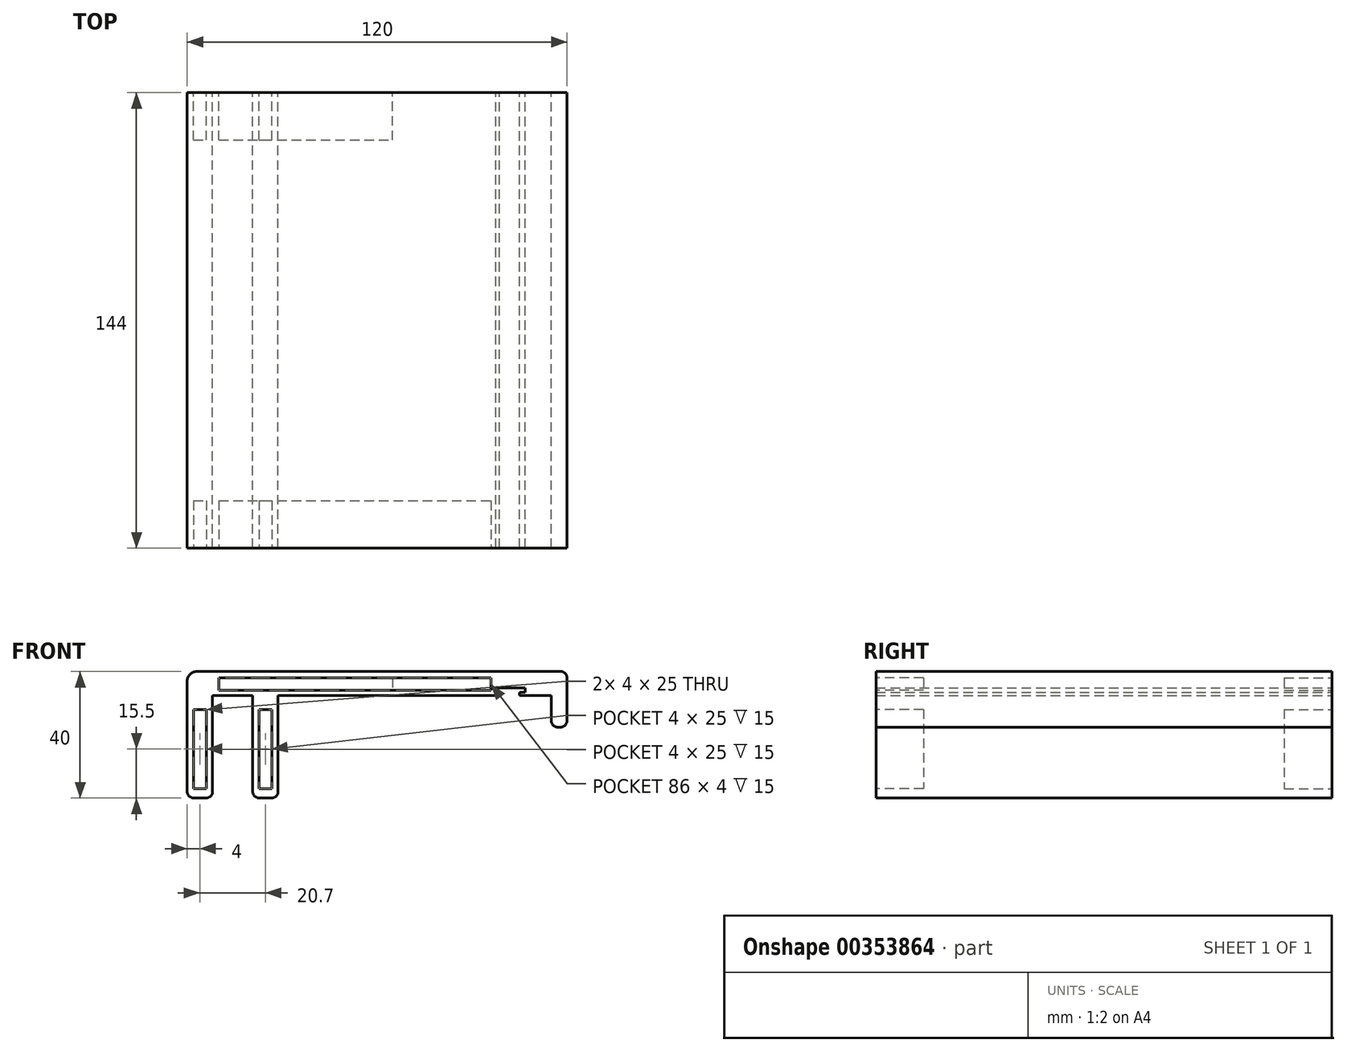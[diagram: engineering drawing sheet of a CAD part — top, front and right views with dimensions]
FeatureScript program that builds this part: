
annotation { "Feature Type Name" : "Feature", "Feature Type Description" : "" }
export const myFeature = defineFeature(function(context is Context, id is Id, definition is map)
    precondition{}
    {
        {
            var Q0;
            Q0=qCreatedBy(makeId("Front.planeOp"),FACE);
            var sketch = newSketch(context, id + "F0", { "sketchPlane" : qUnion([Q0])});
            skLineSegment(sketch, "E0", {"start": v(0, 2) * mm, "end": v(0, 37) * mm});
            skLineSegment(sketch, "E1", {"start": v(3, 40) * mm, "end": v(118, 40) * mm});
            skLineSegment(sketch, "E2", {"start": v(105, 32.4) * mm, "end": v(105, 33.4) * mm});
            skLineSegment(sketch, "E3", {"start": v(105, 33.4) * mm, "end": v(106.75, 33.4) * mm});
            skLineSegment(sketch, "E4", {"start": v(106.75, 33.4) * mm, "end": v(106.75, 34.8) * mm});
            skLineSegment(sketch, "E5", {"start": v(106.75, 34.8) * mm, "end": v(97.45, 34.8) * mm});
            skLineSegment(sketch, "E6", {"start": v(97.45, 34.8) * mm, "end": v(97.45, 33.4) * mm});
            skLineSegment(sketch, "E7", {"start": v(97.45, 33.4) * mm, "end": v(98.7, 33.4) * mm});
            skLineSegment(sketch, "E8", {"start": v(98.7, 33.4) * mm, "end": v(98.7, 32.4) * mm});
            skLineSegment(sketch, "E9", {"start": v(98.7, 32.4) * mm, "end": v(28.7, 32.4) * mm});
            skLineSegment(sketch, "E10", {"start": v(28.7, 32.4) * mm, "end": v(28.7, 2) * mm});
            skLineSegment(sketch, "E11", {"start": v(26.7, 0) * mm, "end": v(22.7, 0) * mm});
            skLineSegment(sketch, "E12", {"start": v(20.7, 2) * mm, "end": v(20.7, 32.4) * mm});
            skLineSegment(sketch, "E13", {"start": v(20.7, 32.4) * mm, "end": v(8, 32.4) * mm});
            skLineSegment(sketch, "E14", {"start": v(8, 32.4) * mm, "end": v(8, 2) * mm});
            skLineSegment(sketch, "E15", {"start": v(6, 0) * mm, "end": v(2, 0) * mm});
            skLineSegment(sketch, "E16", {"start": v(105, 32.4) * mm, "end": v(120, 32.4) * mm});
            skLineSegment(sketch, "E17", {"start": v(120, 38) * mm, "end": v(120, 32.4) * mm});
            skLineSegment(sketch, "E18", {"start": v(120, 32.4) * mm, "end": v(120, 24.4) * mm});
            skLineSegment(sketch, "E19", {"start": v(118, 22.4) * mm, "end": v(117, 22.4) * mm});
            skLineSegment(sketch, "E20", {"start": v(115, 24.4) * mm, "end": v(115, 32.4) * mm});
            skPoint(sketch, "E21.visualSharp", {"position": v(0, 40) * mm});
            skArc(sketch, "E21.filletArc", {"start": v(3, 40) * mm, "mid": v(0.88, 39.12) * mm, "end": v(0, 37) * mm});
            skPoint(sketch, "E22.visualSharp", {"position": v(0, 0) * mm});
            skArc(sketch, "E22.filletArc", {"start": v(0, 2) * mm, "mid": v(0.59, 0.59) * mm, "end": v(2, 0) * mm});
            skPoint(sketch, "E23.visualSharp", {"position": v(8, 0) * mm});
            skArc(sketch, "E23.filletArc", {"start": v(6, 0) * mm, "mid": v(7.41, 0.59) * mm, "end": v(8, 2) * mm});
            skPoint(sketch, "E24.visualSharp", {"position": v(20.7, 0) * mm});
            skArc(sketch, "E24.filletArc", {"start": v(20.7, 2) * mm, "mid": v(21.29, 0.59) * mm, "end": v(22.7, 0) * mm});
            skPoint(sketch, "E25.visualSharp", {"position": v(28.7, 0) * mm});
            skArc(sketch, "E25.filletArc", {"start": v(26.7, 0) * mm, "mid": v(28.11, 0.59) * mm, "end": v(28.7, 2) * mm});
            skPoint(sketch, "E26.visualSharp", {"position": v(120, 22.4) * mm});
            skArc(sketch, "E26.filletArc", {"start": v(118, 22.4) * mm, "mid": v(119.41, 23) * mm, "end": v(120, 24.4) * mm});
            skPoint(sketch, "E27.visualSharp", {"position": v(115, 22.4) * mm});
            skArc(sketch, "E27.filletArc", {"start": v(115, 24.4) * mm, "mid": v(115.59, 23) * mm, "end": v(117, 22.4) * mm});
            skPoint(sketch, "E28.visualSharp", {"position": v(120, 40) * mm});
            skArc(sketch, "E28.filletArc", {"start": v(120, 38) * mm, "mid": v(119.41, 39.41) * mm, "end": v(118, 40) * mm});
            skSolve(sketch);
        }
        {
            var Q0;
            Q0=makeQuery(id+"F0.imprint","IMPRINT",FACE,{"disambiguationData":[TD([[makeQuery(id+"F0.imprint","IMPRINT",EDGE,{"derivedFrom":sQuery(id+"F0.wireOp",EDGE,"E0")}),-1.0]])]});
            var Q1;
            {var subQ1=sQuery(id+"F0.wireOp",EDGE,"E18");Q1=makeQuery(id+"F0.imprint","IMPRINT",FACE,{"disambiguationData":[TD([[makeQuery(id+"F0.imprint","IMPRINT",EDGE,{"derivedFrom":subQ1}),-1.0]])]});}
            extrude(context, id + "F1", {"entities" : qUnion([Q0, Q1]), "depth" : 144 * mm});
        }
        {
            var Q0;
            Q0=makeQuery(id+"F1.opExtrude","CAP_FACE",FACE,{"disambiguationData":[OSD([sQuery(id+"F0.wireOp",EDGE,"E0"),sQuery(id+"F0.wireOp",EDGE,"E1"),sQuery(id+"F0.wireOp",EDGE,"E2"),sQuery(id+"F0.wireOp",EDGE,"E3"),sQuery(id+"F0.wireOp",EDGE,"E4"),sQuery(id+"F0.wireOp",EDGE,"E5"),sQuery(id+"F0.wireOp",EDGE,"E6"),sQuery(id+"F0.wireOp",EDGE,"E7"),sQuery(id+"F0.wireOp",EDGE,"E8"),sQuery(id+"F0.wireOp",EDGE,"E9"),sQuery(id+"F0.wireOp",EDGE,"E10"),sQuery(id+"F0.wireOp",EDGE,"E11"),sQuery(id+"F0.wireOp",EDGE,"E12"),sQuery(id+"F0.wireOp",EDGE,"E13"),sQuery(id+"F0.wireOp",EDGE,"E14"),sQuery(id+"F0.wireOp",EDGE,"E15"),sQuery(id+"F0.wireOp",EDGE,"E16"),sQuery(id+"F0.wireOp",EDGE,"E17"),sQuery(id+"F0.wireOp",EDGE,"E18"),sQuery(id+"F0.wireOp",EDGE,"E19"),sQuery(id+"F0.wireOp",EDGE,"E20"),sQuery(id+"F0.wireOp",EDGE,"E21.filletArc"),sQuery(id+"F0.wireOp",EDGE,"E22.filletArc"),sQuery(id+"F0.wireOp",EDGE,"E23.filletArc"),sQuery(id+"F0.wireOp",EDGE,"E24.filletArc"),sQuery(id+"F0.wireOp",EDGE,"E25.filletArc"),sQuery(id+"F0.wireOp",EDGE,"E26.filletArc"),sQuery(id+"F0.wireOp",EDGE,"E27.filletArc"),sQuery(id+"F0.wireOp",EDGE,"E28.filletArc")])],"isStart":false});
            var sketch = newSketch(context, id + "F2", { "sketchPlane" : qUnion([Q0])});
            skLineSegment(sketch, "E29.bottom", {"start": v(10, 38) * mm, "end": v(96, 38) * mm});
            skLineSegment(sketch, "E29.top", {"start": v(10, 34) * mm, "end": v(96, 34) * mm});
            skLineSegment(sketch, "E29.left", {"start": v(10, 38) * mm, "end": v(10, 34) * mm});
            skLineSegment(sketch, "E29.right", {"start": v(96, 38) * mm, "end": v(96, 34) * mm});
            skLineSegment(sketch, "E30.bottom", {"start": v(2, 28) * mm, "end": v(6, 28) * mm});
            skLineSegment(sketch, "E30.top", {"start": v(2, 3) * mm, "end": v(6, 3) * mm});
            skLineSegment(sketch, "E30.left", {"start": v(2, 28) * mm, "end": v(2, 3) * mm});
            skLineSegment(sketch, "E30.right", {"start": v(6, 28) * mm, "end": v(6, 3) * mm});
            skLineSegment(sketch, "E31.bottom", {"start": v(22.7, 28) * mm, "end": v(26.7, 28) * mm});
            skLineSegment(sketch, "E31.top", {"start": v(22.7, 3) * mm, "end": v(26.7, 3) * mm});
            skLineSegment(sketch, "E31.left", {"start": v(22.7, 28) * mm, "end": v(22.7, 3) * mm});
            skLineSegment(sketch, "E31.right", {"start": v(26.7, 28) * mm, "end": v(26.7, 3) * mm});
            skSolve(sketch);
        }
        {
            var Q0;
            Q0=makeQuery(id+"F2.imprint","IMPRINT",FACE,{"disambiguationData":[TD([[makeQuery(id+"F2.imprint","IMPRINT",EDGE,{"derivedFrom":sQuery(id+"F2.wireOp",EDGE,"E29.bottom")}),-1.0]])]});
            var Q1;
            Q1=makeQuery(id+"F2.imprint","IMPRINT",FACE,{"disambiguationData":[TD([[makeQuery(id+"F2.imprint","IMPRINT",EDGE,{"derivedFrom":sQuery(id+"F2.wireOp",EDGE,"E30.bottom")}),-1.0]])]});
            var Q2;
            Q2=makeQuery(id+"F2.imprint","IMPRINT",FACE,{"disambiguationData":[TD([[makeQuery(id+"F2.imprint","IMPRINT",EDGE,{"derivedFrom":sQuery(id+"F2.wireOp",EDGE,"E31.bottom")}),-1.0]])]});
            extrude(context, id + "F3", {"entities" : qUnion([Q0, Q1, Q2]), "operationType" : NewBodyOperationType.REMOVE, "oppositeDirection" : true, "depth" : 15 * mm});
        }
        {
            var Q0;
            Q0=qCreatedBy(makeId("Front.planeOp"),FACE);
            var sketch = newSketch(context, id + "F4", { "sketchPlane" : qUnion([Q0])});
            skLineSegment(sketch, "E32.bottom", {"start": v(10, 38) * mm, "end": v(64.92, 38) * mm});
            skLineSegment(sketch, "E32.top", {"start": v(10, 34) * mm, "end": v(64.92, 34) * mm});
            skLineSegment(sketch, "E32.left", {"start": v(10, 38) * mm, "end": v(10, 34) * mm});
            skLineSegment(sketch, "E32.right", {"start": v(64.92, 38) * mm, "end": v(64.92, 34) * mm});
            skLineSegment(sketch, "E33.bottom", {"start": v(2, 28) * mm, "end": v(6, 28) * mm});
            skLineSegment(sketch, "E33.top", {"start": v(2, 3) * mm, "end": v(6, 3) * mm});
            skLineSegment(sketch, "E33.left", {"start": v(2, 28) * mm, "end": v(2, 3) * mm});
            skLineSegment(sketch, "E33.right", {"start": v(6, 28) * mm, "end": v(6, 3) * mm});
            skLineSegment(sketch, "E34.bottom", {"start": v(22.7, 28) * mm, "end": v(26.7, 28) * mm});
            skLineSegment(sketch, "E34.top", {"start": v(22.7, 3) * mm, "end": v(26.7, 3) * mm});
            skLineSegment(sketch, "E34.left", {"start": v(22.7, 28) * mm, "end": v(22.7, 3) * mm});
            skLineSegment(sketch, "E34.right", {"start": v(26.7, 28) * mm, "end": v(26.7, 3) * mm});
            skSolve(sketch);
        }
        {
            var Q0;
            Q0=qSketchRegion(id+"F4",true);
            extrude(context, id + "F5", {"entities" : qUnion([Q0]), "operationType" : NewBodyOperationType.REMOVE, "depth" : 15 * mm});
        }
    });
